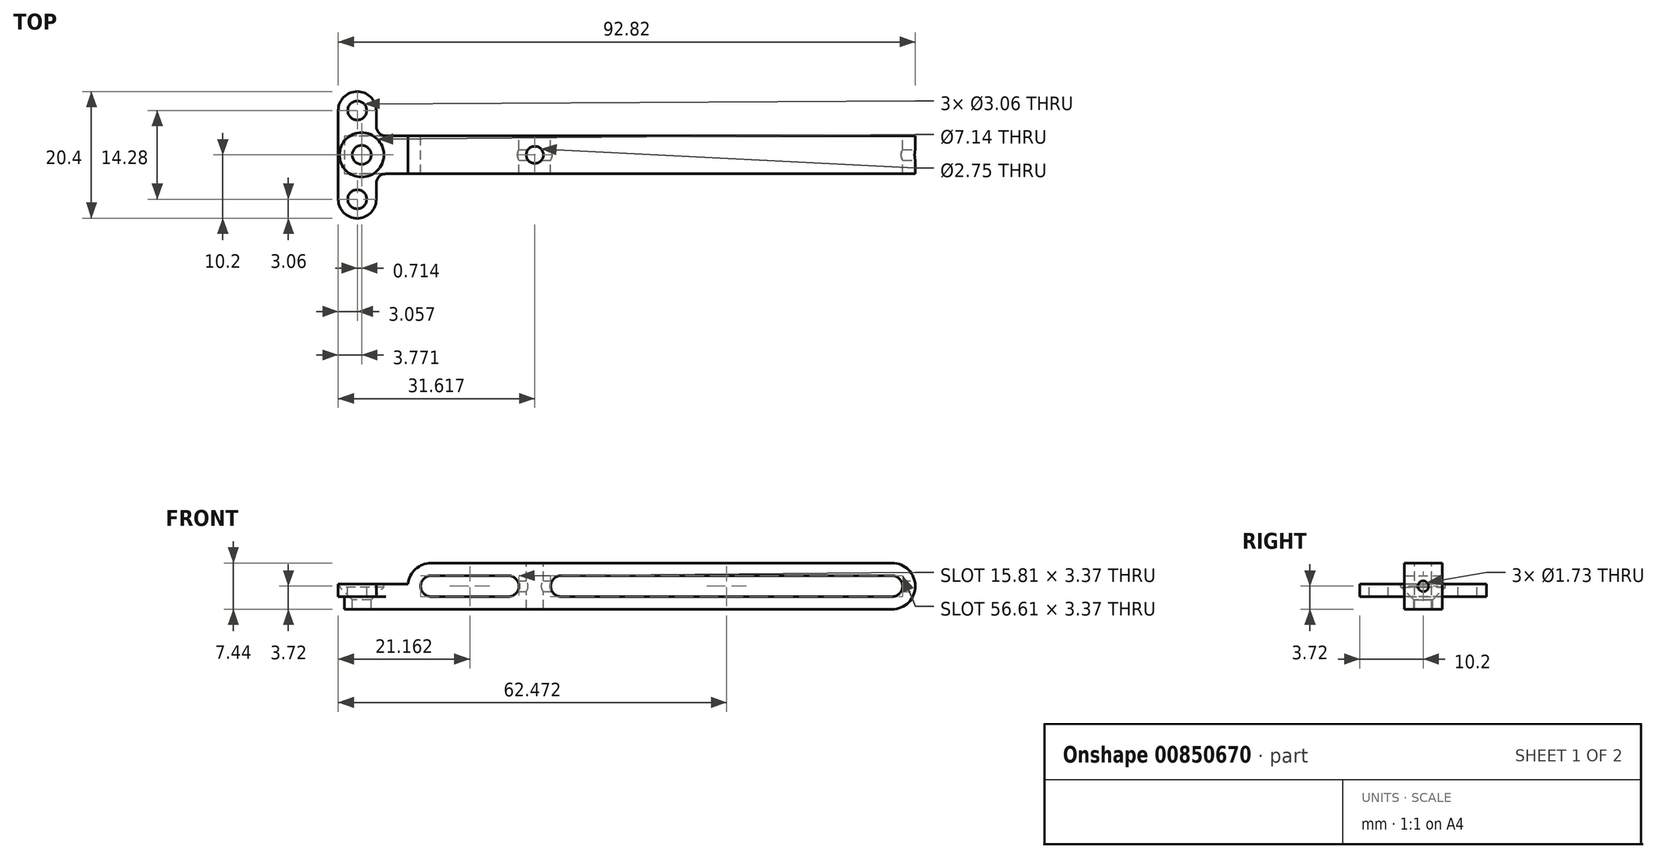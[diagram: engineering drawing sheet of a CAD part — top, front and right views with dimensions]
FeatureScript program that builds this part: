
annotation { "Feature Type Name" : "Feature", "Feature Type Description" : "" }
export const myFeature = defineFeature(function(context is Context, id is Id, definition is map)
    precondition{}
    {
        {
            var Q0;
            Q0=qCreatedBy(makeId("Front.planeOp"),FACE);
            var sketch = newSketch(context, id + "F0", { "sketchPlane" : qUnion([Q0])});
            skLineSegment(sketch, "E0", {"start": v(0, 0) * mm, "end": v(72.7, 0) * mm, "construction": true});
            skArc(sketch, "E1.0.startCap", {"start": v(0, -3.65) * mm, "mid": v(-3.65, 0) * mm, "end": v(0, 3.65) * mm});
            skArc(sketch, "E1.0.endCap", {"start": v(72.7, 3.65) * mm, "mid": v(76.35, 0) * mm, "end": v(72.7, -3.65) * mm});
            skLineSegment(sketch, "E1.0.left", {"start": v(0, 3.65) * mm, "end": v(72.7, 3.65) * mm});
            skLineSegment(sketch, "E1.0.right", {"start": v(0, -3.65) * mm, "end": v(72.7, -3.65) * mm});
            skLineSegment(sketch, "E2.0", {"start": v(0, -1.65) * mm, "end": v(12.2, -1.65) * mm});
            skArc(sketch, "E2.1", {"start": v(0, -1.65) * mm, "mid": v(-1.65, 0) * mm, "end": v(0, 1.65) * mm});
            skLineSegment(sketch, "E2.2", {"start": v(0, 1.65) * mm, "end": v(12.2, 1.65) * mm});
            skArc(sketch, "E2.3", {"start": v(72.7, 1.65) * mm, "mid": v(74.35, 0) * mm, "end": v(72.7, -1.65) * mm});
            skArc(sketch, "E3", {"start": v(12.2, -1.65) * mm, "mid": v(13.85, 0) * mm, "end": v(12.2, 1.65) * mm});
            skArc(sketch, "E4", {"start": v(20.5, 1.65) * mm, "mid": v(18.85, 0) * mm, "end": v(20.5, -1.65) * mm});
            skLineSegment(sketch, "E5", {"start": v(16.35, -3.65) * mm, "end": v(16.35, 3.65) * mm, "construction": true});
            skLineSegment(sketch, "E6.trimOffspring", {"start": v(20.5, -1.65) * mm, "end": v(72.7, -1.65) * mm});
            skLineSegment(sketch, "E7.trimOffspring", {"start": v(20.5, 1.65) * mm, "end": v(72.7, 1.65) * mm});
            skSolve(sketch);
        }
        {
            var Q0;
            Q0 = qSketchRegion(id + "F0", true);
            extrude(context, id + "F1", {"entities" : qUnion([Q0]), "endBound" : BoundingType.SYMMETRIC, "depth" : 6 * mm, "offsetDistance" : 25 * mm});
        }
        {
            var Q0;
            Q0=makeQuery(id+"F1.opExtrude","CAP_FACE",FACE,{"disambiguationData":[OSD([sQuery(id+"F0.wireOp",EDGE,"E1.0.startCap"),sQuery(id+"F0.wireOp",EDGE,"E1.0.endCap"),sQuery(id+"F0.wireOp",EDGE,"E1.0.left"),sQuery(id+"F0.wireOp",EDGE,"E1.0.right"),sQuery(id+"F0.wireOp",EDGE,"E2.0"),sQuery(id+"F0.wireOp",EDGE,"E2.1"),sQuery(id+"F0.wireOp",EDGE,"E2.2"),sQuery(id+"F0.wireOp",EDGE,"E2.3")])],"isStart":false});
            var sketch = newSketch(context, id + "F2", { "sketchPlane" : qUnion([Q0])});
            skLineSegment(sketch, "E8.bottom", {"start": v(0, -3.65) * mm, "end": v(-13.65, -3.65) * mm});
            skLineSegment(sketch, "E8.top", {"start": v(-3.63, 0.35) * mm, "end": v(-13.65, 0.35) * mm});
            skLineSegment(sketch, "E8.right", {"start": v(-13.65, -3.65) * mm, "end": v(-13.65, 0.35) * mm});
            skArc(sketch, "E9.0", {"start": v(0, -3.65) * mm, "mid": v(-2.7, -2.45) * mm, "end": v(-3.63, 0.35) * mm});
            skPoint(sketch, "E10.orphan", {"position": v(0, 3.65) * mm});
            skSolve(sketch);
        }
        {
            var Q0;
            Q0 = qSketchRegion(id + "F2", true);
            var Q1;
            Q1=makeQuery(id+"F1.opExtrude","CAP_FACE",FACE,{"disambiguationData":[OSD([sQuery(id+"F0.wireOp",EDGE,"E1.0.startCap"),sQuery(id+"F0.wireOp",EDGE,"E1.0.endCap"),sQuery(id+"F0.wireOp",EDGE,"E1.0.left"),sQuery(id+"F0.wireOp",EDGE,"E1.0.right"),sQuery(id+"F0.wireOp",EDGE,"E2.0"),sQuery(id+"F0.wireOp",EDGE,"E2.1"),sQuery(id+"F0.wireOp",EDGE,"E2.2"),sQuery(id+"F0.wireOp",EDGE,"E2.3")])],"isStart":true});
            extrude(context, id + "F3", {"entities" : qUnion([Q0]), "operationType" : NewBodyOperationType.ADD, "endBound" : BoundingType.UP_TO_SURFACE, "oppositeDirection" : true, "depth" : 25 * mm, "endBoundEntityFace" : qUnion([Q1]), "offsetDistance" : 25 * mm});
        }
        {
            var Q0;
            Q0=makeQuery(id+"F3.opExtrude","SWEPT_FACE",FACE,{"disambiguationData":[OSD([sQuery(id+"F2.wireOp",EDGE,"E8.top")])]});
            var sketch = newSketch(context, id + "F4", { "sketchPlane" : qUnion([Q0])});
            skLineSegment(sketch, "E11", {"start": v(0, 0) * mm, "end": v(-11.65, 0) * mm, "construction": true});
            skLineSegment(sketch, "E12", {"start": v(-11.65, -7) * mm, "end": v(-11.65, 7) * mm, "construction": true});
            skArc(sketch, "E13.0.startCap", {"start": v(-8.65, -7) * mm, "mid": v(-11.65, -10) * mm, "end": v(-14.65, -7) * mm});
            skArc(sketch, "E13.0.endCap", {"start": v(-14.65, 7) * mm, "mid": v(-11.65, 10) * mm, "end": v(-8.65, 7) * mm});
            skLineSegment(sketch, "E13.0.left", {"start": v(-14.65, -7) * mm, "end": v(-14.65, 7) * mm});
            skLineSegment(sketch, "E13.0.right", {"start": v(-8.65, -7) * mm, "end": v(-8.65, 7) * mm});
            skCircle(sketch, "E14", {"center": v(-10.95, 0) * mm, "radius": 3.5 * mm, "construction": true});
            skSolve(sketch);
        }
        {
            var Q0;
            Q0 = qSketchRegion(id + "F4", true);
            extrude(context, id + "F5", {"entities" : qUnion([Q0]), "operationType" : NewBodyOperationType.ADD, "oppositeDirection" : true, "depth" : 2 * mm, "offsetDistance" : 25 * mm});
        }
        {
            var Q0;
            Q0=makeQuery(id+"F5.boolean.opBoolean","MERGE",FACE,{"derivedFrom":[makeQuery(id+"F3.opExtrude","SWEPT_FACE",FACE,{"disambiguationData":[OSD([sQuery(id+"F2.wireOp",EDGE,"E8.top")])]}),makeQuery(id+"F5.opExtrude","CAP_FACE",FACE,{"disambiguationData":[OSD([sQuery(id+"F4.wireOp",EDGE,"E13.0.startCap"),sQuery(id+"F4.wireOp",EDGE,"E13.0.endCap"),sQuery(id+"F4.wireOp",EDGE,"E13.0.left"),sQuery(id+"F4.wireOp",EDGE,"E13.0.right")])],"isStart":true})]});
            var sketch = newSketch(context, id + "F6", { "sketchPlane" : qUnion([Q0])});
            skCircle(sketch, "E15.0", {"center": v(-10.95, 0) * mm, "radius": 3.5 * mm});
            skSolve(sketch);
        }
        {
            var Q0;
            Q0 = qSketchRegion(id + "F6", true);
            extrude(context, id + "F7", {"entities" : qUnion([Q0]), "operationType" : NewBodyOperationType.REMOVE, "oppositeDirection" : true, "depth" : .5 * mm, "offsetDistance" : 25 * mm});
        }
        {
            var Q0;
            Q0=makeQuery(id+"F7.boolean.opBoolean","COPY",FACE,{"derivedFrom":makeQuery(id+"F7.opExtrude","CAP_FACE",FACE,{"disambiguationData":[OSD([sQuery(id+"F6.wireOp",EDGE,"E15.0")])],"isStart":false})});
            var sketch = newSketch(context, id + "F8", { "sketchPlane" : qUnion([Q0])});
            skPoint(sketch, "E16", {"position": v(-10.95, 0) * mm});
            skSolve(sketch);
        }
        {
            var Q0;
            Q0=sQuery(id+"F8.wireOp",VERTEX,"E16");
            var Q1;
            Q1=makeQuery(id+"F1.opExtrude","SWEPT_BODY",BODY,{"disambiguationData":[OSD([sQuery(id+"F0.wireOp",EDGE,"E1.0.startCap"),sQuery(id+"F0.wireOp",EDGE,"E1.0.endCap"),sQuery(id+"F0.wireOp",EDGE,"E1.0.left"),sQuery(id+"F0.wireOp",EDGE,"E1.0.right"),sQuery(id+"F0.wireOp",EDGE,"E2.0"),sQuery(id+"F0.wireOp",EDGE,"E2.1"),sQuery(id+"F0.wireOp",EDGE,"E2.2"),sQuery(id+"F0.wireOp",EDGE,"E2.3")])]});
            hole(context, id + "F9", {"style" : HoleStyle.C_SINK, "endStyle" : HoleEndStyle.THROUGH, "holeDiameter" : 3 * mm, "cSinkDiameter" : 7 * mm, "cSinkAngle" : 90 * degree, "majorDiameter" : 5 * mm, "isTappedThrough" : true, "tappedDepth" : 12 * mm, "tapClearance" : 3, "startFromSketch" : true, "locations" : qUnion([Q0]), "scope" : qUnion([Q1])});
        }
        {
            var Q0;
            Q0=sQuery(id+"F4.wireOp",VERTEX,"E12.end");
            var Q1;
            Q1=sQuery(id+"F4.wireOp",VERTEX,"E12.start");
            var Q2;
            Q2=makeQuery(id+"F1.opExtrude","SWEPT_BODY",BODY,{"disambiguationData":[OSD([sQuery(id+"F0.wireOp",EDGE,"E1.0.startCap"),sQuery(id+"F0.wireOp",EDGE,"E1.0.endCap"),sQuery(id+"F0.wireOp",EDGE,"E1.0.left"),sQuery(id+"F0.wireOp",EDGE,"E1.0.right"),sQuery(id+"F0.wireOp",EDGE,"E2.0"),sQuery(id+"F0.wireOp",EDGE,"E2.1"),sQuery(id+"F0.wireOp",EDGE,"E2.2"),sQuery(id+"F0.wireOp",EDGE,"E2.3"),sQuery(id+"F0.wireOp",EDGE,"E3"),sQuery(id+"F0.wireOp",EDGE,"E4"),sQuery(id+"F0.wireOp",EDGE,"E6.trimOffspring"),sQuery(id+"F0.wireOp",EDGE,"E7.trimOffspring")])]});
            hole(context, id + "F10", {"style" : HoleStyle.SIMPLE, "endStyle" : HoleEndStyle.THROUGH, "standardTappedOrClearance" : lookupTablePath({ "standard" : "ISO", "size" : "3", "type" : "Drilled" }), "standardBlindInLast" : lookupTablePath({ "standard" : "ISO", "size" : "3", "type" : "Drilled" }), "holeDiameter" : 3 * mm, "majorDiameter" : 5 * mm, "isTappedThrough" : true, "tappedDepth" : 12 * mm, "tapClearance" : 3, "startFromSketch" : true, "locations" : qUnion([Q0, Q1]), "scope" : qUnion([Q2])});
        }
        {
            var Q0;
            Q0=makeQuery(id+"F5.boolean.opBoolean","INTERSECT",EDGE,{"derivedFrom":[makeQuery(id+"F3.boolean.opBoolean","MERGE",FACE,{"derivedFrom":[makeQuery(id+"F1.opExtrude","CAP_FACE",FACE,{"disambiguationData":[OSD([sQuery(id+"F0.wireOp",EDGE,"E1.0.startCap"),sQuery(id+"F0.wireOp",EDGE,"E1.0.endCap"),sQuery(id+"F0.wireOp",EDGE,"E1.0.left"),sQuery(id+"F0.wireOp",EDGE,"E1.0.right"),sQuery(id+"F0.wireOp",EDGE,"E2.0"),sQuery(id+"F0.wireOp",EDGE,"E2.1"),sQuery(id+"F0.wireOp",EDGE,"E2.2"),sQuery(id+"F0.wireOp",EDGE,"E2.3")])],"isStart":false}),makeQuery(id+"F3.opExtrude","CAP_FACE",FACE,{"disambiguationData":[OSD([sQuery(id+"F2.wireOp",EDGE,"E8.bottom"),sQuery(id+"F2.wireOp",EDGE,"E8.top"),sQuery(id+"F2.wireOp",EDGE,"E8.right"),sQuery(id+"F2.wireOp",EDGE,"E9.0")])],"isStart":true})]}),makeQuery(id+"F5.opExtrude","SWEPT_FACE",FACE,{"disambiguationData":[OSD([sQuery(id+"F4.wireOp",EDGE,"E13.0.right")])]})]});
            var Q1;
            {var subQ0=sQuery(id+"F0.wireOp",EDGE,"E2.3");var subQ1=sQuery(id+"F0.wireOp",EDGE,"E2.2");var subQ2=sQuery(id+"F0.wireOp",EDGE,"E2.1");var subQ3=sQuery(id+"F0.wireOp",EDGE,"E2.0");var subQ4=sQuery(id+"F0.wireOp",EDGE,"E1.0.right");var subQ5=sQuery(id+"F0.wireOp",EDGE,"E1.0.left");var subQ6=sQuery(id+"F0.wireOp",EDGE,"E1.0.endCap");var subQ7=sQuery(id+"F0.wireOp",EDGE,"E1.0.startCap");Q1=makeQuery(id+"F5.boolean.opBoolean","INTERSECT",EDGE,{"derivedFrom":[makeQuery(id+"F3.boolean.opBoolean","MERGE",FACE,{"derivedFrom":[makeQuery(id+"F1.opExtrude","CAP_FACE",FACE,{"disambiguationData":[OSD([subQ7,subQ6,subQ5,subQ4,subQ3,subQ2,subQ1,subQ0])],"isStart":true}),makeQuery(id+"F3.opExtrude","CAP_FACE",FACE,{"disambiguationData":[OSD([subQ7,subQ6,subQ5,subQ4,subQ3,subQ2,subQ1,subQ0])],"isStart":false})]}),makeQuery(id+"F5.opExtrude","SWEPT_FACE",FACE,{"disambiguationData":[OSD([sQuery(id+"F4.wireOp",EDGE,"E13.0.right")])]})]});}
            var Q2;
            Q2=makeQuery(id+"F3.opExtrude","SWEPT_EDGE",EDGE,{"disambiguationData":[OSD([sQuery(id+"F0.wireOp",EDGE,"E1.0.startCap"),sQuery(id+"F2.wireOp",EDGE,"E8.top"),sQuery(id+"F2.wireOp",EDGE,"E9.0")])]});
            fillet(context, id + "F11", {"entities" : qUnion([Q0, Q1, Q2]), "radius" : 1.5 * mm, "tangentPropagation" : true, "allowEdgeOverflow" : false});
        }
        {
            var Q0;
            Q0=makeQuery(id+"F1.opExtrude","CAP_EDGE",EDGE,{"disambiguationData":[OSD([sQuery(id+"F0.wireOp",EDGE,"E1.0.endCap")])],"isStart":false});
            cPoint(context, id + "F12", {"entities" : qUnion([Q0]), "parameter" : 0.5});
        }
        {
            var Q0;
            Q0=qCreatedBy(makeId("Right.planeOp"),FACE);
            var Q1;
            Q1 = qCreatedBy(id + "F12" ,VERTEX);
            cPlane(context, id + "F13", {"entities" : qUnion([Q0, Q1]), "cplaneType" : CPlaneType.PLANE_POINT, "offset" : 25 * mm, "width" : 150 * mm, "height" : 150 * mm});
        }
        {
            var Q0;
            Q0=qCreatedBy(id+"F13.planeOp",FACE);
            var sketch = newSketch(context, id + "F14", { "sketchPlane" : qUnion([Q0])});
            skCircle(sketch, "E17", {"center": v(0, 0) * mm, "radius": 0.85 * mm});
            skSolve(sketch);
        }
        {
            var Q0;
            Q0 = qSketchRegion(id + "F14", true);
            var Q1;
            Q1=makeQuery(id+"F1.opExtrude","SWEPT_FACE",FACE,{"disambiguationData":[OSD([sQuery(id+"F0.wireOp",EDGE,"E3")])]});
            extrude(context, id + "F15", {"entities" : qUnion([Q0]), "operationType" : NewBodyOperationType.REMOVE, "endBound" : BoundingType.UP_TO_SURFACE, "oppositeDirection" : true, "depth" : 25 * mm, "endBoundEntityFace" : qUnion([Q1]), "offsetDistance" : 25 * mm});
        }
        {
            var Q0;
            Q0=makeQuery(id+"F1.opExtrude","SWEPT_FACE",FACE,{"disambiguationData":[OSD([sQuery(id+"F0.wireOp",EDGE,"E1.0.left")])]});
            var sketch = newSketch(context, id + "F16", { "sketchPlane" : qUnion([Q0])});
            skPoint(sketch, "E18", {"position": v(16.35, 0) * mm});
            skSolve(sketch);
        }
        {
            var Q0;
            Q0=sQuery(id+"F16.wireOp",VERTEX,"E18");
            var Q1;
            Q1=makeQuery(id+"F1.opExtrude","SWEPT_BODY",BODY,{"disambiguationData":[OSD([sQuery(id+"F0.wireOp",EDGE,"E1.0.startCap"),sQuery(id+"F0.wireOp",EDGE,"E1.0.endCap"),sQuery(id+"F0.wireOp",EDGE,"E1.0.left"),sQuery(id+"F0.wireOp",EDGE,"E1.0.right"),sQuery(id+"F0.wireOp",EDGE,"E2.0"),sQuery(id+"F0.wireOp",EDGE,"E2.1"),sQuery(id+"F0.wireOp",EDGE,"E2.2"),sQuery(id+"F0.wireOp",EDGE,"E2.3"),sQuery(id+"F0.wireOp",EDGE,"E3"),sQuery(id+"F0.wireOp",EDGE,"E4"),sQuery(id+"F0.wireOp",EDGE,"E6.trimOffspring"),sQuery(id+"F0.wireOp",EDGE,"E7.trimOffspring")])]});
            hole(context, id + "F17", {"style" : HoleStyle.SIMPLE, "endStyle" : HoleEndStyle.THROUGH, "holeDiameter" : 2.7 * mm, "majorDiameter" : 3 * mm, "isTappedThrough" : true, "tappedDepth" : 7.3 * mm, "tapClearance" : 3, "startFromSketch" : true, "locations" : qUnion([Q0]), "scope" : qUnion([Q1])});
        }
        {
            var Q0;
            Q0=makeQuery(id+"F1.opExtrude","SWEPT_BODY",BODY,{"disambiguationData":[OSD([sQuery(id+"F0.wireOp",EDGE,"E1.0.startCap"),sQuery(id+"F0.wireOp",EDGE,"E1.0.endCap"),sQuery(id+"F0.wireOp",EDGE,"E1.0.left"),sQuery(id+"F0.wireOp",EDGE,"E1.0.right"),sQuery(id+"F0.wireOp",EDGE,"E2.0"),sQuery(id+"F0.wireOp",EDGE,"E2.1"),sQuery(id+"F0.wireOp",EDGE,"E2.2"),sQuery(id+"F0.wireOp",EDGE,"E2.3"),sQuery(id+"F0.wireOp",EDGE,"E3"),sQuery(id+"F0.wireOp",EDGE,"E4"),sQuery(id+"F0.wireOp",EDGE,"E6.trimOffspring"),sQuery(id+"F0.wireOp",EDGE,"E7.trimOffspring")])]});
            var Q1;
            Q1=qCreatedBy(makeId("Origin.pointOp"),VERTEX);
            transform(context, id + "F18", {"entities" : qUnion([Q0]), "transformType" : TransformType.SCALE_UNIFORMLY, "scale" : 1.02, "scalePoint" : qUnion([Q1]), "makeCopy" : false});
        }
    });
